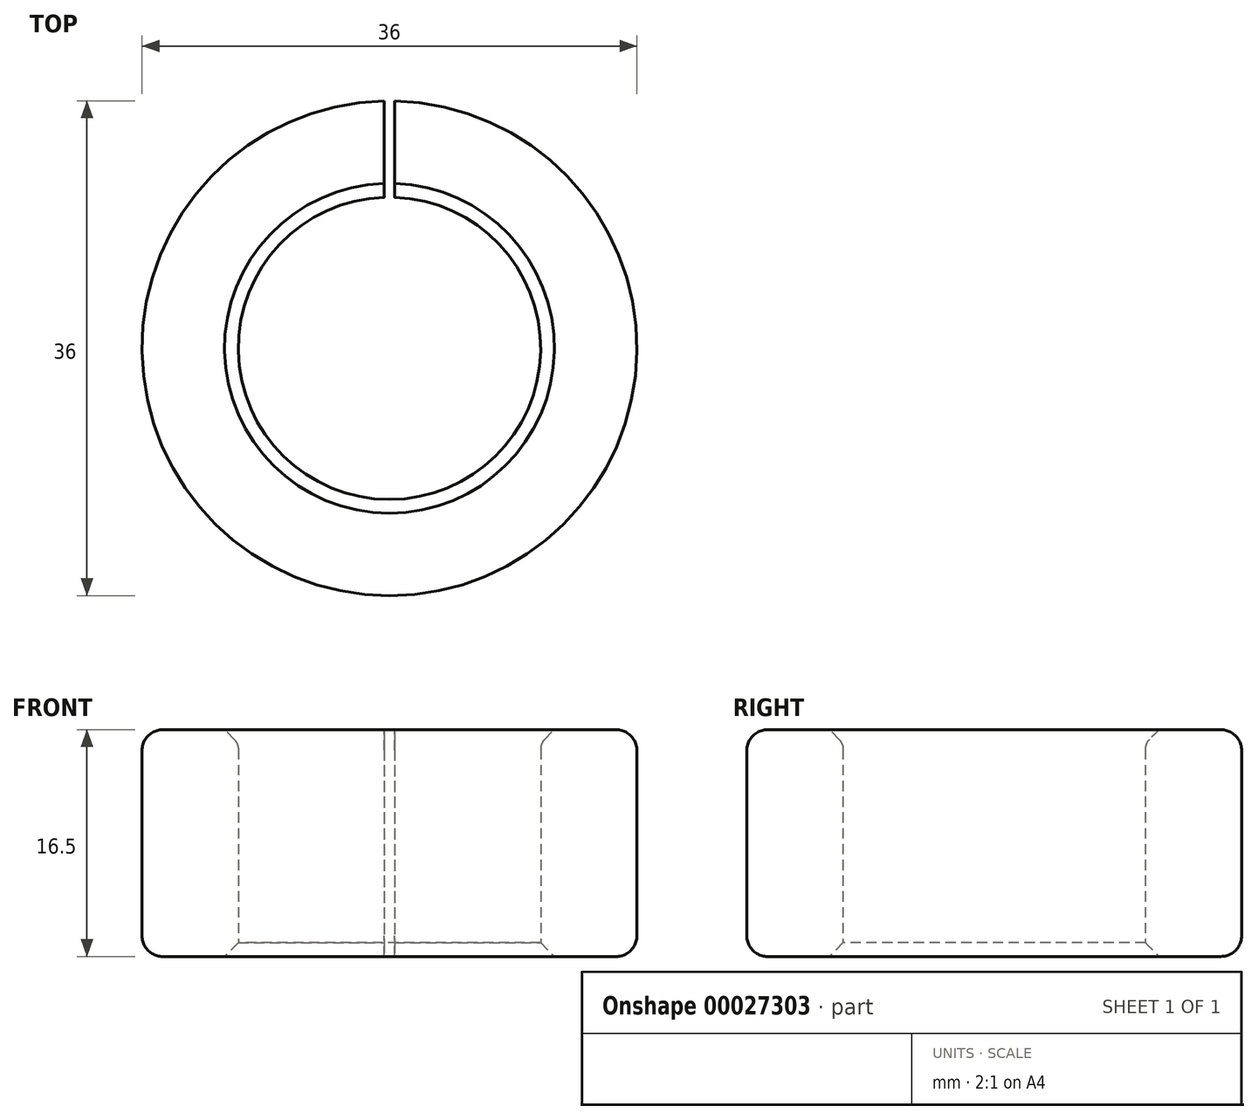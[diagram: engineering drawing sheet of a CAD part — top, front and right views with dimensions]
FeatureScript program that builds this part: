
annotation { "Feature Type Name" : "Feature", "Feature Type Description" : "" }
export const myFeature = defineFeature(function(context is Context, id is Id, definition is map)
    precondition{}
    {
        {
            var Q0;
            Q0=qCreatedBy(makeId("Top.planeOp"),FACE);
            var sketch = newSketch(context, id + "F0", { "sketchPlane" : qUnion([Q0])});
            skCircle(sketch, "E0", {"center": v(0, 0) * mm, "radius": 11 * mm});
            skCircle(sketch, "E1", {"center": v(0, 0) * mm, "radius": 18 * mm});
            skSolve(sketch);
        }
        {
            var Q0;
            Q0=makeQuery(id+"F0.imprint","IMPRINT",FACE,{"disambiguationData":[TD([[makeQuery(id+"F0.imprint","IMPRINT",EDGE,{"derivedFrom":sQuery(id+"F0.wireOp",EDGE,"E0")}),-1.0]])]});
            extrude(context, id + "F1", {"entities" : qUnion([Q0]), "depth" : 9.5 * mm});
        }
        {
            var Q0;
            {var subQ0=sQuery(id+"F0.wireOp",EDGE,"E0");var subQ1=sQuery(id+"F0.wireOp",EDGE,"E1");Q0=makeQuery(id+"FzDQCP4s0yXR5Fl_1.boolean.opBoolean","SPLIT",FACE,{"disambiguationData":[TD([makeQuery(id+"FzDQCP4s0yXR5Fl_1.opExtrude","SWEPT_FACE",FACE,{"disambiguationData":[OSD([sQuery(id+"F0BN2LC1fxE3Ahz_1.wireOp",EDGE,"7d1290e8-91e9-487d-a68e-7fe6769417ec.right")])]})])],"derivedFrom":makeQuery(id+"F1.opExtrude","CAP_FACE",FACE,{"disambiguationData":[OSD([subQ0,subQ1])],"isStart":false})});}
            var sketch = newSketch(context, id + "F2", { "sketchPlane" : qUnion([Q0])});
            skCircle(sketch, "E2", {"center": v(0, 0) * mm, "radius": 18 * mm});
            skCircle(sketch, "E3", {"center": v(0, 0) * mm, "radius": 11 * mm});
            skSolve(sketch);
        }
        {
            var Q0;
            Q0=makeQuery(id+"F2.imprint","IMPRINT",FACE,{"disambiguationData":[TD([[makeQuery(id+"F2.imprint","IMPRINT",EDGE,{"derivedFrom":sQuery(id+"F2.wireOp",EDGE,"E2")}),1.0]])]});
            extrude(context, id + "F3", {"entities" : qUnion([Q0]), "operationType" : NewBodyOperationType.ADD, "depth" : 3.5 * mm});
        }
        {
            var Q0;
            {var subQ0=sQuery(id+"F0.wireOp",EDGE,"E0");var subQ1=sQuery(id+"F0.wireOp",EDGE,"E1");Q0=makeQuery(id+"FzDQCP4s0yXR5Fl_1.boolean.opBoolean","SPLIT",FACE,{"disambiguationData":[TD([makeQuery(id+"FzDQCP4s0yXR5Fl_1.opExtrude","SWEPT_FACE",FACE,{"disambiguationData":[OSD([sQuery(id+"F0BN2LC1fxE3Ahz_1.wireOp",EDGE,"df38452c-8aee-4457-8b0a-5bbbfc862e17.3.1")])]})])],"derivedFrom":makeQuery(id+"F1.opExtrude","CAP_FACE",FACE,{"disambiguationData":[OSD([subQ0,subQ1])],"isStart":true})});}
            var sketch = newSketch(context, id + "F4", { "sketchPlane" : qUnion([Q0])});
            skCircle(sketch, "E4", {"center": v(0, 0) * mm, "radius": 18 * mm});
            skCircle(sketch, "E5", {"center": v(0, 0) * mm, "radius": 11 * mm});
            skSolve(sketch);
        }
        {
            var Q0;
            Q0=makeQuery(id+"F4.imprint","IMPRINT",FACE,{"disambiguationData":[TD([[makeQuery(id+"F4.imprint","IMPRINT",EDGE,{"disambiguationData":[OD(0.0)],"derivedFrom":sQuery(id+"F4.wireOp",EDGE,"E4")}),1.0]])]});
            var Q1;
            Q1=makeQuery(id+"F4.imprint","IMPRINT",FACE,{"disambiguationData":[TD([[makeQuery(id+"F4.imprint","IMPRINT",EDGE,{"disambiguationData":[OD(1.0)],"derivedFrom":sQuery(id+"F4.wireOp",EDGE,"E4")}),-1.0]])]});
            extrude(context, id + "F5", {"entities" : qUnion([Q0, Q1]), "operationType" : NewBodyOperationType.ADD, "depth" : 3.5 * mm});
        }
        {
            var Q0;
            Q0=makeQuery(id+"F5.opExtrude","CAP_EDGE",EDGE,{"disambiguationData":[OSD([sQuery(id+"F4.wireOp",EDGE,"E4")])],"isStart":false});
            var Q1;
            Q1=makeQuery(id+"F3.opExtrude","CAP_EDGE",EDGE,{"disambiguationData":[OSD([sQuery(id+"F2.wireOp",EDGE,"E2")])],"isStart":false});
            fillet(context, id + "F6", {"entities" : qUnion([Q0, Q1]), "radius" : 1.5 * mm, "tangentPropagation" : true, "allowEdgeOverflow" : false});
        }
        {
            var Q0;
            Q0=makeQuery(id+"F5.opExtrude","CAP_EDGE",EDGE,{"disambiguationData":[OSD([sQuery(id+"F4.wireOp",EDGE,"E5")])],"isStart":false});
            var Q1;
            Q1=makeQuery(id+"F3.opExtrude","CAP_EDGE",EDGE,{"disambiguationData":[OSD([sQuery(id+"F2.wireOp",EDGE,"E3")])],"isStart":false});
            chamfer(context, id + "F7", {"entities" : qUnion([Q0, Q1]), "width" : 1 * mm, "tangentPropagation" : true});
        }
        {
            var Q0;
            {var subQ0=sQuery(id+"F2.wireOp",EDGE,"E3");var subQ1=sQuery(id+"F0.wireOp",EDGE,"E0");var subQ2=makeQuery(id+"F1.opExtrude","SWEPT_FACE",FACE,{"disambiguationData":[OSD([subQ1])]});Q0=makeQuery(id+"F7.opChamfer","BLEND_EDGE",EDGE,{"blendedFrom":[makeQuery(id+"F3.opExtrude","CAP_EDGE",EDGE,{"disambiguationData":[OSD([subQ0])],"isStart":false}),makeQuery(id+"F5.boolean.opBoolean","MERGE",FACE,{"derivedFrom":[makeQuery(id+"F3.boolean.opBoolean","MERGE",FACE,{"derivedFrom":[makeQuery(id+"FzDQCP4s0yXR5Fl_1.boolean.opBoolean","SPLIT",FACE,{"disambiguationData":[TD([makeQuery(id+"FzDQCP4s0yXR5Fl_1.opExtrude","SWEPT_FACE",FACE,{"disambiguationData":[OSD([sQuery(id+"F0BN2LC1fxE3Ahz_1.wireOp",EDGE,"7d1290e8-91e9-487d-a68e-7fe6769417ec.left")])]})])],"derivedFrom":subQ2}),makeQuery(id+"FzDQCP4s0yXR5Fl_1.boolean.opBoolean","SPLIT",FACE,{"disambiguationData":[TD([makeQuery(id+"FzDQCP4s0yXR5Fl_1.opExtrude","SWEPT_FACE",FACE,{"disambiguationData":[OSD([sQuery(id+"F0BN2LC1fxE3Ahz_1.wireOp",EDGE,"7d1290e8-91e9-487d-a68e-7fe6769417ec.right")])]})])],"derivedFrom":subQ2}),makeQuery(id+"FzDQCP4s0yXR5Fl_1.boolean.opBoolean","SPLIT",FACE,{"disambiguationData":[TD([makeQuery(id+"FzDQCP4s0yXR5Fl_1.opExtrude","SWEPT_FACE",FACE,{"disambiguationData":[OSD([sQuery(id+"F0BN2LC1fxE3Ahz_1.wireOp",EDGE,"df38452c-8aee-4457-8b0a-5bbbfc862e17.1.1")])]})])],"derivedFrom":subQ2}),makeQuery(id+"FzDQCP4s0yXR5Fl_1.boolean.opBoolean","SPLIT",FACE,{"disambiguationData":[TD([makeQuery(id+"FzDQCP4s0yXR5Fl_1.opExtrude","SWEPT_FACE",FACE,{"disambiguationData":[OSD([sQuery(id+"F0BN2LC1fxE3Ahz_1.wireOp",EDGE,"df38452c-8aee-4457-8b0a-5bbbfc862e17.2.1")])]})])],"derivedFrom":subQ2}),makeQuery(id+"FzDQCP4s0yXR5Fl_1.boolean.opBoolean","SPLIT",FACE,{"disambiguationData":[TD([makeQuery(id+"FzDQCP4s0yXR5Fl_1.opExtrude","SWEPT_FACE",FACE,{"disambiguationData":[OSD([sQuery(id+"F0BN2LC1fxE3Ahz_1.wireOp",EDGE,"df38452c-8aee-4457-8b0a-5bbbfc862e17.3.1")])]})])],"derivedFrom":subQ2}),makeQuery(id+"FzDQCP4s0yXR5Fl_1.boolean.opBoolean","SPLIT",FACE,{"disambiguationData":[TD([makeQuery(id+"FzDQCP4s0yXR5Fl_1.opExtrude","SWEPT_FACE",FACE,{"disambiguationData":[OSD([sQuery(id+"F0BN2LC1fxE3Ahz_1.wireOp",EDGE,"df38452c-8aee-4457-8b0a-5bbbfc862e17.4.1")])]})])],"derivedFrom":subQ2}),makeQuery(id+"F3.opExtrude","SWEPT_FACE",FACE,{"disambiguationData":[OSD([subQ0])]})]}),makeQuery(id+"F5.opExtrude","SWEPT_FACE",FACE,{"disambiguationData":[OSD([sQuery(id+"F4.wireOp",EDGE,"E5")])]})]})],"blendedInto":[makeQuery(id+"F5.boolean.opBoolean","MERGE",FACE,{"derivedFrom":[makeQuery(id+"F3.boolean.opBoolean","MERGE",FACE,{"derivedFrom":[makeQuery(id+"FzDQCP4s0yXR5Fl_1.boolean.opBoolean","SPLIT",FACE,{"disambiguationData":[TD([makeQuery(id+"FzDQCP4s0yXR5Fl_1.opExtrude","SWEPT_FACE",FACE,{"disambiguationData":[OSD([sQuery(id+"F0BN2LC1fxE3Ahz_1.wireOp",EDGE,"7d1290e8-91e9-487d-a68e-7fe6769417ec.left")])]})])],"derivedFrom":subQ2}),makeQuery(id+"FzDQCP4s0yXR5Fl_1.boolean.opBoolean","SPLIT",FACE,{"disambiguationData":[TD([makeQuery(id+"FzDQCP4s0yXR5Fl_1.opExtrude","SWEPT_FACE",FACE,{"disambiguationData":[OSD([sQuery(id+"F0BN2LC1fxE3Ahz_1.wireOp",EDGE,"7d1290e8-91e9-487d-a68e-7fe6769417ec.right")])]})])],"derivedFrom":subQ2}),makeQuery(id+"FzDQCP4s0yXR5Fl_1.boolean.opBoolean","SPLIT",FACE,{"disambiguationData":[TD([makeQuery(id+"FzDQCP4s0yXR5Fl_1.opExtrude","SWEPT_FACE",FACE,{"disambiguationData":[OSD([sQuery(id+"F0BN2LC1fxE3Ahz_1.wireOp",EDGE,"df38452c-8aee-4457-8b0a-5bbbfc862e17.1.1")])]})])],"derivedFrom":subQ2}),makeQuery(id+"FzDQCP4s0yXR5Fl_1.boolean.opBoolean","SPLIT",FACE,{"disambiguationData":[TD([makeQuery(id+"FzDQCP4s0yXR5Fl_1.opExtrude","SWEPT_FACE",FACE,{"disambiguationData":[OSD([sQuery(id+"F0BN2LC1fxE3Ahz_1.wireOp",EDGE,"df38452c-8aee-4457-8b0a-5bbbfc862e17.2.1")])]})])],"derivedFrom":subQ2}),makeQuery(id+"FzDQCP4s0yXR5Fl_1.boolean.opBoolean","SPLIT",FACE,{"disambiguationData":[TD([makeQuery(id+"FzDQCP4s0yXR5Fl_1.opExtrude","SWEPT_FACE",FACE,{"disambiguationData":[OSD([sQuery(id+"F0BN2LC1fxE3Ahz_1.wireOp",EDGE,"df38452c-8aee-4457-8b0a-5bbbfc862e17.3.1")])]})])],"derivedFrom":subQ2}),makeQuery(id+"FzDQCP4s0yXR5Fl_1.boolean.opBoolean","SPLIT",FACE,{"disambiguationData":[TD([makeQuery(id+"FzDQCP4s0yXR5Fl_1.opExtrude","SWEPT_FACE",FACE,{"disambiguationData":[OSD([sQuery(id+"F0BN2LC1fxE3Ahz_1.wireOp",EDGE,"df38452c-8aee-4457-8b0a-5bbbfc862e17.4.1")])]})])],"derivedFrom":subQ2}),makeQuery(id+"F3.opExtrude","SWEPT_FACE",FACE,{"disambiguationData":[OSD([subQ0])]})]}),makeQuery(id+"F5.opExtrude","SWEPT_FACE",FACE,{"disambiguationData":[OSD([sQuery(id+"F4.wireOp",EDGE,"E5")])]})]})]});}
            fillet(context, id + "F8", {"entities" : qUnion([Q0]), "radius" : 1 * mm, "tangentPropagation" : true, "allowEdgeOverflow" : false});
        }
        {
            var Q0;
            Q0=makeQuery(id+"F3.opExtrude","CAP_FACE",FACE,{"disambiguationData":[OSD([sQuery(id+"F2.wireOp",EDGE,"E2"),sQuery(id+"F2.wireOp",EDGE,"E3")])],"isStart":false});
            var sketch = newSketch(context, id + "F9", { "sketchPlane" : qUnion([Q0])});
            skLineSegment(sketch, "E6.bottom", {"start": v(-0.37, 18.61) * mm, "end": v(0.37, 18.61) * mm});
            skLineSegment(sketch, "E6.top", {"start": v(-0.37, 10.61) * mm, "end": v(0.37, 10.61) * mm});
            skLineSegment(sketch, "E6.left", {"start": v(-0.37, 18.61) * mm, "end": v(-0.37, 10.61) * mm});
            skLineSegment(sketch, "E6.right", {"start": v(0.37, 18.61) * mm, "end": v(0.38, 10.61) * mm});
            skSolve(sketch);
        }
        {
            var Q0;
            Q0 = qSketchRegion(id + "F9", true);
            extrude(context, id + "F10", {"entities" : qUnion([Q0]), "operationType" : NewBodyOperationType.REMOVE, "endBound" : BoundingType.THROUGH_ALL, "oppositeDirection" : true, "depth" : 25 * mm});
        }
    });
